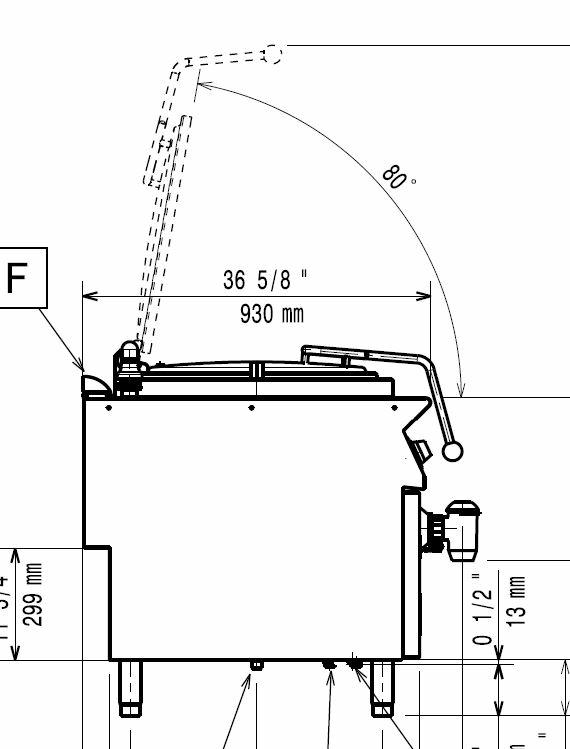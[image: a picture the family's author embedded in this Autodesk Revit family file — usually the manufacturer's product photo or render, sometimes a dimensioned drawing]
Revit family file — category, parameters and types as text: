
# Revit family: QF_ELECTROLUXPROFESSIONAL_391612_E9NNFTBAMEI
name_source: partatom
category: Attrezzature speciali
units: mm (PartAtom-declared; Revit-internal decimal feet)

## family parameters
Basato su piano di lavoro = No
Condiviso = No
Punto di calcolo locali = No
Quota connettore circolare = Usa diametro
Sempre verticale = Sì
Taglio con vuoti quando caricato = No
Tipo di parte = Normale

## types (1)
- Standard
    Accessory = Sì
    Cold Water Size = 1"
    Compressed Air Pressure = 0.00 psi
    Compressed Air Size = 0"
    Compressed Air Volume = 0 GPM
    Condensate Return Size = 0"
    Cycle = 60 Hz
    Depth Actual = 930 mm  [stored 3.05118 ft]
    Descrizione = 150LT GAS BOILING PAN-DIRECT HEATING-60HZ - QMARK
    Direct Waste Size = 2"
    Gas Input Pressure = 0.8
    Gas KW = 24
    Gas Size = 1"
    HP = 0.1 HP
    Height Actual = 850 mm  [stored 2.78871 ft]
    Hot Water Size = 1"
    Item Number = 391612
    Length Actual = 800 mm  [stored 2.62467 ft]
    Modello = E9NNFTBAMEI
    Phase = 1
    Produttore = Electrolux Professional
    Prospetto di default = 0 mm  [stored 0 ft]
    Refrigerant Compressor Remote = Sì
    Refrigeration Liquid Line Size = 0 mm  [stored 0 ft]
    Refrigeration Suction Line Size = 0 mm  [stored 0 ft]
    Steam Consumption per Hour = 0
    Steam Supply Maximum Pressure = 0.00 psi
    Steam Supply Minimum Pressure = 0.00 psi
    Steam Supply Size = 0"
    URL = https://www.electroluxprofessional.com
    URL Manufacturer = https://www.electroluxprofessional.com
    Volts = 220 V
    Watts = 100 W
    Weight = 135.00 kg

note: source unit labels omitted for Gas Input Pressure — the stored unit's dimension contradicts the parameter name (converter mislabeling)

note: [stored X ft] marks values corroborated as IEEE doubles in the binary element streams (Revit-internal decimal feet)

## geometry (parser evidence)
native form markers: Blend x9, Sweep x2
no freeform markers — native parametric forms only
